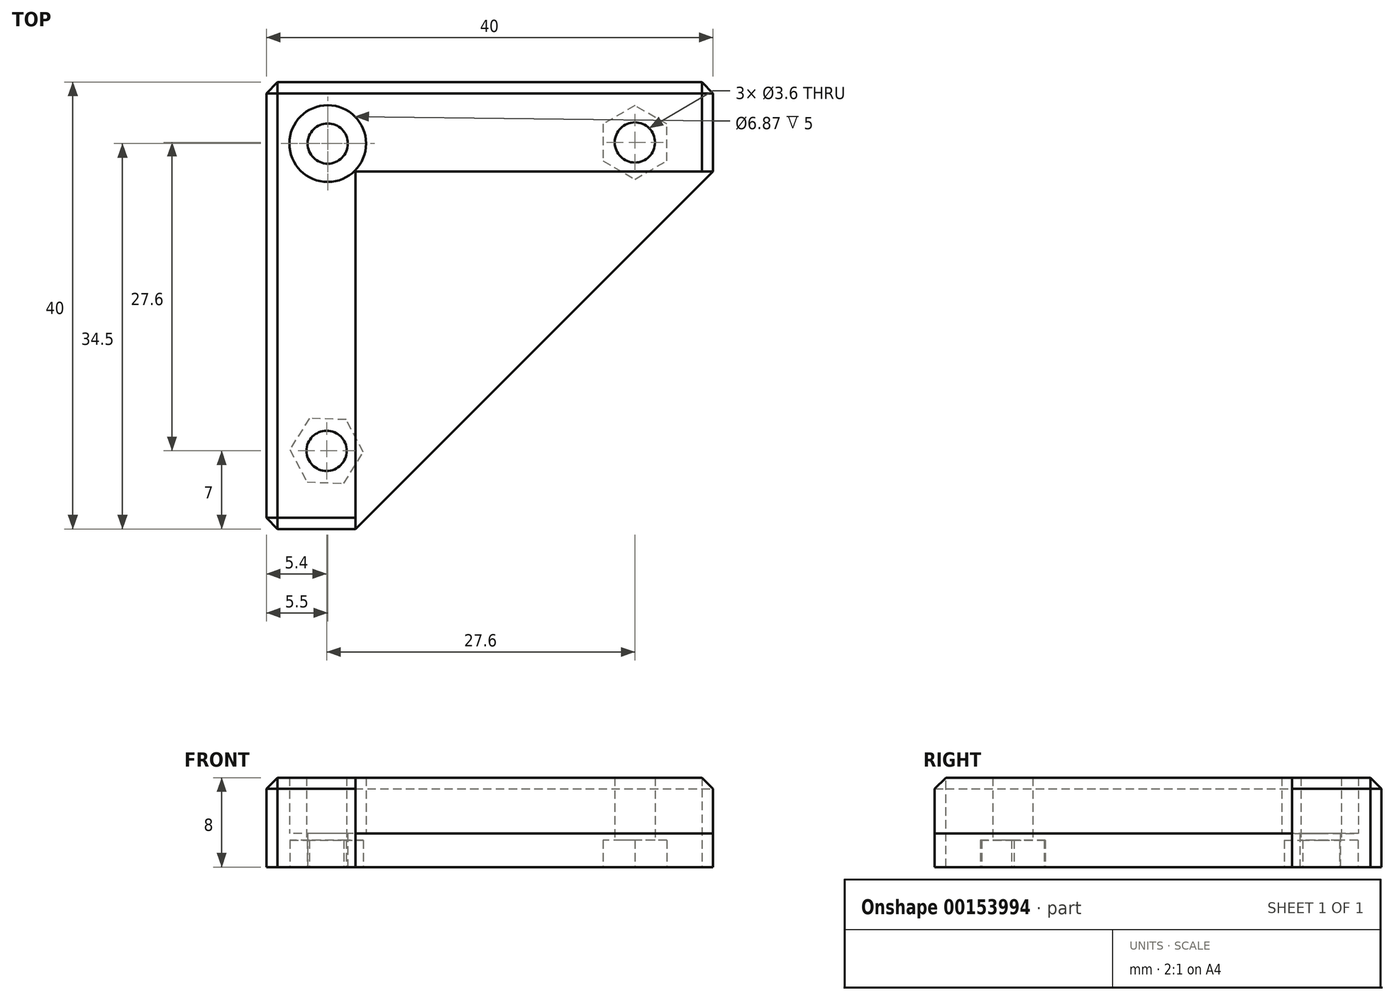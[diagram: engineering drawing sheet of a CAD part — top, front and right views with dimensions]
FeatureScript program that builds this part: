
annotation { "Feature Type Name" : "Feature", "Feature Type Description" : "" }
export const myFeature = defineFeature(function(context is Context, id is Id, definition is map)
    precondition{}
    {
        {
            var Q0;
            Q0=qCreatedBy(makeId("Top.planeOp"),FACE);
            var sketch = newSketch(context, id + "F0", { "sketchPlane" : qUnion([Q0])});
            skCircle(sketch, "E0", {"center": v(0, 0) * mm, "radius": 1.8 * mm});
            skLineSegment(sketch, "E1", {"start": v(-5.5, 5.5) * mm, "end": v(34.5, 5.5) * mm});
            skLineSegment(sketch, "E2", {"start": v(34.5, 5.5) * mm, "end": v(34.5, -2.5) * mm});
            skLineSegment(sketch, "E3", {"start": v(34.5, -2.5) * mm, "end": v(2.5, -34.5) * mm});
            skLineSegment(sketch, "E4", {"start": v(2.5, -34.5) * mm, "end": v(-5.5, -34.5) * mm});
            skLineSegment(sketch, "E5", {"start": v(-5.5, -34.5) * mm, "end": v(-5.5, 5.5) * mm});
            skLineSegment(sketch, "E6", {"start": v(34.5, -2.5) * mm, "end": v(2.5, -2.5) * mm});
            skLineSegment(sketch, "E7", {"start": v(2.5, -2.5) * mm, "end": v(2.5, -34.5) * mm});
            skCircle(sketch, "E8", {"center": v(0, 0) * mm, "radius": 3.44 * mm});
            skCircle(sketch, "E9", {"center": v(27.5, 0.1) * mm, "radius": 1.8 * mm});
            skCircle(sketch, "E10", {"center": v(-0.1, -27.5) * mm, "radius": 1.8 * mm});
            skSolve(sketch);
        }
        {
            var Q0;
            Q0=makeQuery(id+"F0.imprint","IMPRINT",FACE,{"disambiguationData":[TD([[makeQuery(id+"F0.imprint","IMPRINT",EDGE,{"derivedFrom":sQuery(id+"F0.wireOp",EDGE,"E1")}),-1.0]])]});
            extrude(context, id + "F1", {"entities" : qUnion([Q0]), "depth" : 8 * mm});
        }
        {
            var Q0;
            Q0=makeQuery(id+"F0.imprint","IMPRINT",FACE,{"disambiguationData":[TD([[makeQuery(id+"F0.imprint","IMPRINT",EDGE,{"derivedFrom":sQuery(id+"F0.wireOp",EDGE,"E3")}),-1.0]])]});
            var Q1;
            Q1=makeQuery(id+"F0.imprint","IMPRINT",FACE,{"disambiguationData":[TD([[makeQuery(id+"F0.imprint","IMPRINT",EDGE,{"derivedFrom":sQuery(id+"F0.wireOp",EDGE,"E0")}),-1.0]])]});
            extrude(context, id + "F2", {"entities" : qUnion([Q0, Q1]), "operationType" : NewBodyOperationType.ADD, "depth" : 3 * mm});
        }
        {
            var Q0;
            {var subQ0=sQuery(id+"F0.wireOp",EDGE,"E7");var subQ1=sQuery(id+"F0.wireOp",EDGE,"E6");var subQ2=sQuery(id+"F0.wireOp",EDGE,"E8");Q0=makeQuery(id+"F2.boolean.opBoolean","MERGE",FACE,{"derivedFrom":[makeQuery(id+"F1.opExtrude","CAP_FACE",FACE,{"disambiguationData":[OSD([sQuery(id+"F0.wireOp",EDGE,"E1"),sQuery(id+"F0.wireOp",EDGE,"E2"),sQuery(id+"F0.wireOp",EDGE,"E4"),sQuery(id+"F0.wireOp",EDGE,"E5"),subQ1,subQ0,subQ2,sQuery(id+"F0.wireOp",EDGE,"E9"),sQuery(id+"F0.wireOp",EDGE,"E10")])],"isStart":true}),makeQuery(id+"F2.opExtrude","CAP_FACE",FACE,{"disambiguationData":[OSD([sQuery(id+"F0.wireOp",EDGE,"E0"),subQ2])],"isStart":true}),makeQuery(id+"F2.opExtrude","CAP_FACE",FACE,{"disambiguationData":[OSD([sQuery(id+"F0.wireOp",EDGE,"E3"),subQ1,subQ0])],"isStart":true})]});}
            var sketch = newSketch(context, id + "F3", { "sketchPlane" : qUnion([Q0])});
            skCircle(sketch, "E11.cCircle", {"center": v(-0.1, 27.5) * mm, "radius": 2.85 * mm, "construction": true});
            skLineSegment(sketch, "E11.0", {"start": v(1.64, 24.7) * mm, "end": v(-1.64, 24.6) * mm});
            skLineSegment(sketch, "E11.1", {"start": v(-1.64, 24.6) * mm, "end": v(-3.39, 27.38) * mm});
            skLineSegment(sketch, "E11.2", {"start": v(-3.39, 27.38) * mm, "end": v(-1.84, 30.3) * mm});
            skLineSegment(sketch, "E11.3", {"start": v(-1.84, 30.3) * mm, "end": v(1.44, 30.4) * mm});
            skLineSegment(sketch, "E11.4", {"start": v(1.44, 30.4) * mm, "end": v(3.19, 27.62) * mm});
            skLineSegment(sketch, "E11.5", {"start": v(3.19, 27.62) * mm, "end": v(1.64, 24.7) * mm});
            skPoint(sketch, "E11.0.midPoint", {"position": v(0, 24.65) * mm});
            skCircle(sketch, "E12.cCircle", {"center": v(27.5, -0.1) * mm, "radius": 2.85 * mm, "construction": true});
            skLineSegment(sketch, "E12.0", {"start": v(24.65, -1.75) * mm, "end": v(24.65, 1.55) * mm});
            skLineSegment(sketch, "E12.1", {"start": v(24.65, 1.55) * mm, "end": v(27.5, 3.2) * mm});
            skLineSegment(sketch, "E12.2", {"start": v(27.5, 3.2) * mm, "end": v(30.35, 1.55) * mm});
            skLineSegment(sketch, "E12.3", {"start": v(30.35, 1.55) * mm, "end": v(30.35, -1.75) * mm});
            skLineSegment(sketch, "E12.4", {"start": v(30.35, -1.75) * mm, "end": v(27.5, -3.4) * mm});
            skLineSegment(sketch, "E12.5", {"start": v(27.5, -3.4) * mm, "end": v(24.65, -1.75) * mm});
            skPoint(sketch, "E12.0.midPoint", {"position": v(24.65, -0.1) * mm});
            skSolve(sketch);
        }
        {
            var Q0;
            Q0=makeQuery(id+"F3.imprint","IMPRINT",FACE,{"disambiguationData":[TD([[makeQuery(id+"F3.imprint","IMPRINT",EDGE,{"derivedFrom":sQuery(id+"F3.wireOp",EDGE,"E11.0")}),-1.0]])]});
            var Q1;
            Q1=makeQuery(id+"F3.imprint","IMPRINT",FACE,{"disambiguationData":[TD([[makeQuery(id+"F3.imprint","IMPRINT",EDGE,{"derivedFrom":sQuery(id+"F3.wireOp",EDGE,"E12.0")}),-1.0]])]});
            extrude(context, id + "F4", {"entities" : qUnion([Q0, Q1]), "operationType" : NewBodyOperationType.REMOVE, "oppositeDirection" : true, "depth" : 2.4 * mm});
        }
        {
            var Q0;
            Q0=makeQuery(id+"F1.opExtrude","SWEPT_EDGE",EDGE,{"disambiguationData":[OSD([sQuery(id+"F0.wireOp",EDGE,"E1"),sQuery(id+"F0.wireOp",EDGE,"E5")])]});
            var Q1;
            Q1=makeQuery(id+"F1.opExtrude","SWEPT_EDGE",EDGE,{"disambiguationData":[OSD([sQuery(id+"F0.wireOp",EDGE,"E4"),sQuery(id+"F0.wireOp",EDGE,"E5")])]});
            var Q2;
            Q2=makeQuery(id+"F1.opExtrude","SWEPT_EDGE",EDGE,{"disambiguationData":[OSD([sQuery(id+"F0.wireOp",EDGE,"E1"),sQuery(id+"F0.wireOp",EDGE,"E2")])]});
            var Q3;
            Q3=makeQuery(id+"F1.opExtrude","CAP_EDGE",EDGE,{"disambiguationData":[OSD([sQuery(id+"F0.wireOp",EDGE,"E1")])],"isStart":false});
            var Q4;
            Q4=makeQuery(id+"F1.opExtrude","CAP_EDGE",EDGE,{"disambiguationData":[OSD([sQuery(id+"F0.wireOp",EDGE,"E5")])],"isStart":false});
            var Q5;
            Q5=makeQuery(id+"F1.opExtrude","CAP_EDGE",EDGE,{"disambiguationData":[OSD([sQuery(id+"F0.wireOp",EDGE,"E4")])],"isStart":false});
            var Q6;
            Q6=makeQuery(id+"F1.opExtrude","CAP_EDGE",EDGE,{"disambiguationData":[OSD([sQuery(id+"F0.wireOp",EDGE,"E2")])],"isStart":false});
            chamfer(context, id + "F5", {"entities" : qUnion([Q0, Q1, Q2, Q3, Q4, Q5, Q6]), "width" : 1 * mm, "tangentPropagation" : true});
        }
    });
